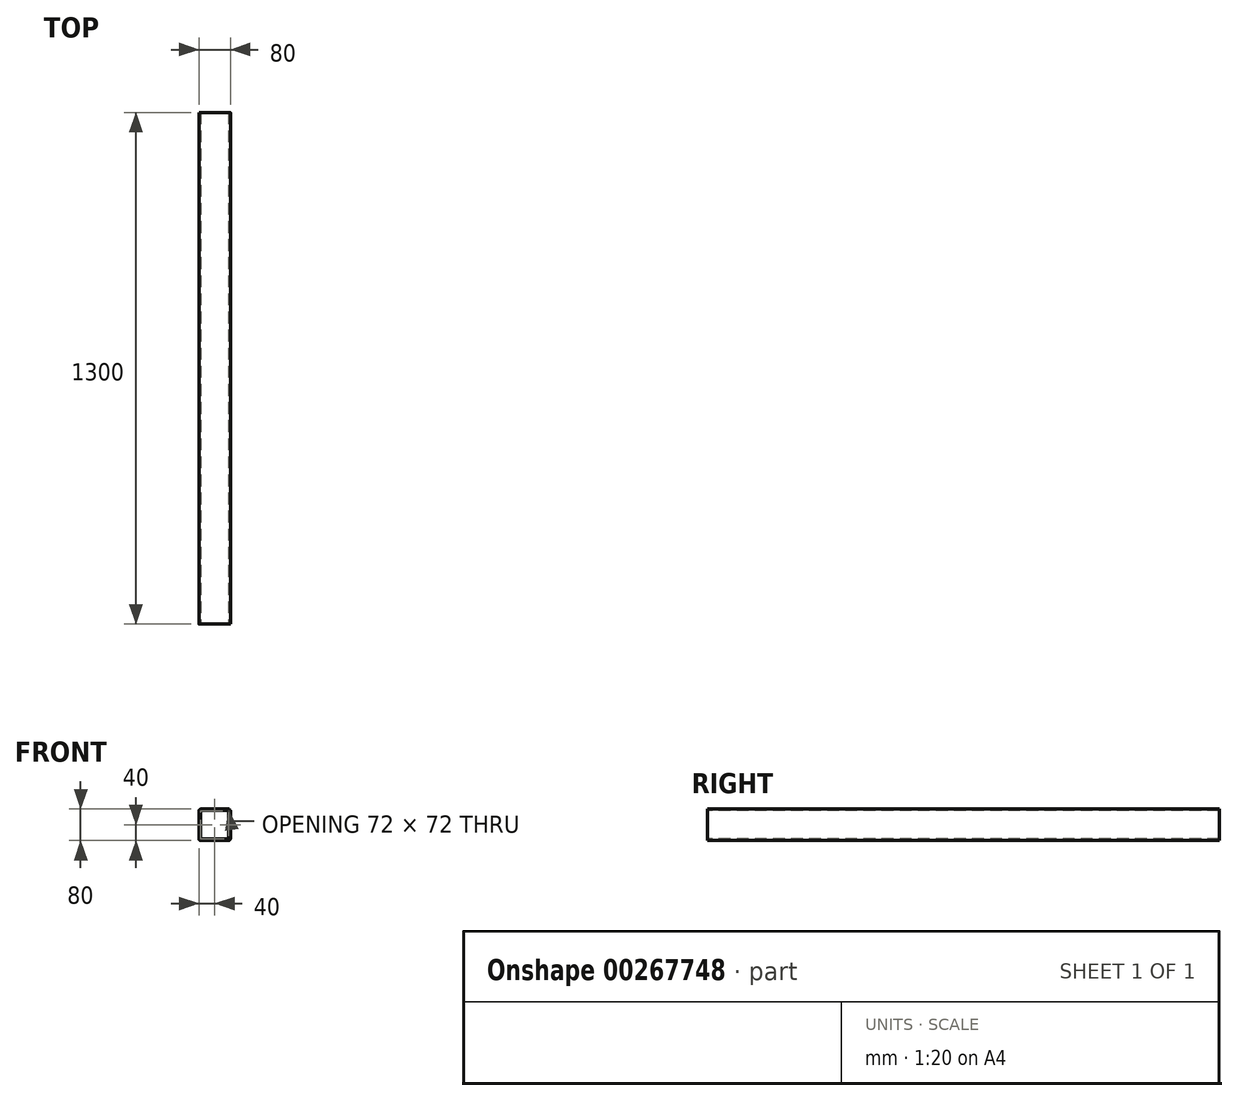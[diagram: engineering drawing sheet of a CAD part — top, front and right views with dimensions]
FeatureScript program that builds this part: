
annotation { "Feature Type Name" : "Feature", "Feature Type Description" : "" }
export const myFeature = defineFeature(function(context is Context, id is Id, definition is map)
    precondition{}
    {
        {
            var Q0;
            Q0=qCreatedBy(makeId("Front.planeOp"),FACE);
            var sketch = newSketch(context, id + "F0", { "sketchPlane" : qUnion([Q0])});
            skLineSegment(sketch, "E0.bottom", {"start": v(35, 40) * mm, "end": v(-35, 40) * mm});
            skLineSegment(sketch, "E0.top", {"start": v(35, -40) * mm, "end": v(-35, -40) * mm});
            skLineSegment(sketch, "E0.left", {"start": v(40, 35) * mm, "end": v(40, -35) * mm});
            skLineSegment(sketch, "E0.right", {"start": v(-40, 35) * mm, "end": v(-40, -35) * mm});
            skPoint(sketch, "E0.middle", {"position": v(0, 0) * mm});
            skPoint(sketch, "E1.visualSharp", {"position": v(-40, 40) * mm});
            skArc(sketch, "E1.filletArc", {"start": v(-35, 40) * mm, "mid": v(-38.54, 38.54) * mm, "end": v(-40, 35) * mm});
            skPoint(sketch, "E2.visualSharp", {"position": v(40, 40) * mm});
            skArc(sketch, "E2.filletArc", {"start": v(40, 35) * mm, "mid": v(38.54, 38.54) * mm, "end": v(35, 40) * mm});
            skPoint(sketch, "E3.visualSharp", {"position": v(40, -40) * mm});
            skArc(sketch, "E3.filletArc", {"start": v(35, -40) * mm, "mid": v(38.54, -38.54) * mm, "end": v(40, -35) * mm});
            skPoint(sketch, "E4.visualSharp", {"position": v(-40, -40) * mm});
            skArc(sketch, "E4.filletArc", {"start": v(-40, -35) * mm, "mid": v(-38.54, -38.54) * mm, "end": v(-35, -40) * mm});
            skArc(sketch, "E5.0", {"start": v(-35, 36) * mm, "mid": v(-35.7, 35.7) * mm, "end": v(-36, 35) * mm});
            skLineSegment(sketch, "E5.1", {"start": v(35, 36) * mm, "end": v(-35, 36) * mm});
            skLineSegment(sketch, "E5.2", {"start": v(-36, 35) * mm, "end": v(-36, -35) * mm});
            skArc(sketch, "E5.3", {"start": v(36, 35) * mm, "mid": v(35.7, 35.7) * mm, "end": v(35, 36) * mm});
            skArc(sketch, "E5.4", {"start": v(-36, -35) * mm, "mid": v(-35.7, -35.7) * mm, "end": v(-35, -36) * mm});
            skLineSegment(sketch, "E5.5", {"start": v(35, -36) * mm, "end": v(-35, -36) * mm});
            skArc(sketch, "E5.6", {"start": v(35, -36) * mm, "mid": v(35.7, -35.7) * mm, "end": v(36, -35) * mm});
            skLineSegment(sketch, "E5.7", {"start": v(36, 35) * mm, "end": v(36, -35) * mm});
            skSolve(sketch);
        }
        {
            var Q0;
            Q0=makeQuery(id+"F0.imprint","IMPRINT",FACE,{"disambiguationData":[TD([[makeQuery(id+"F0.imprint","IMPRINT",EDGE,{"derivedFrom":sQuery(id+"F0.wireOp",EDGE,"E0.bottom")}),1.0]])]});
            extrude(context, id + "F1", {"entities" : qUnion([Q0]), "oppositeDirection" : true, "depth" : 1300 * mm});
        }
    });
